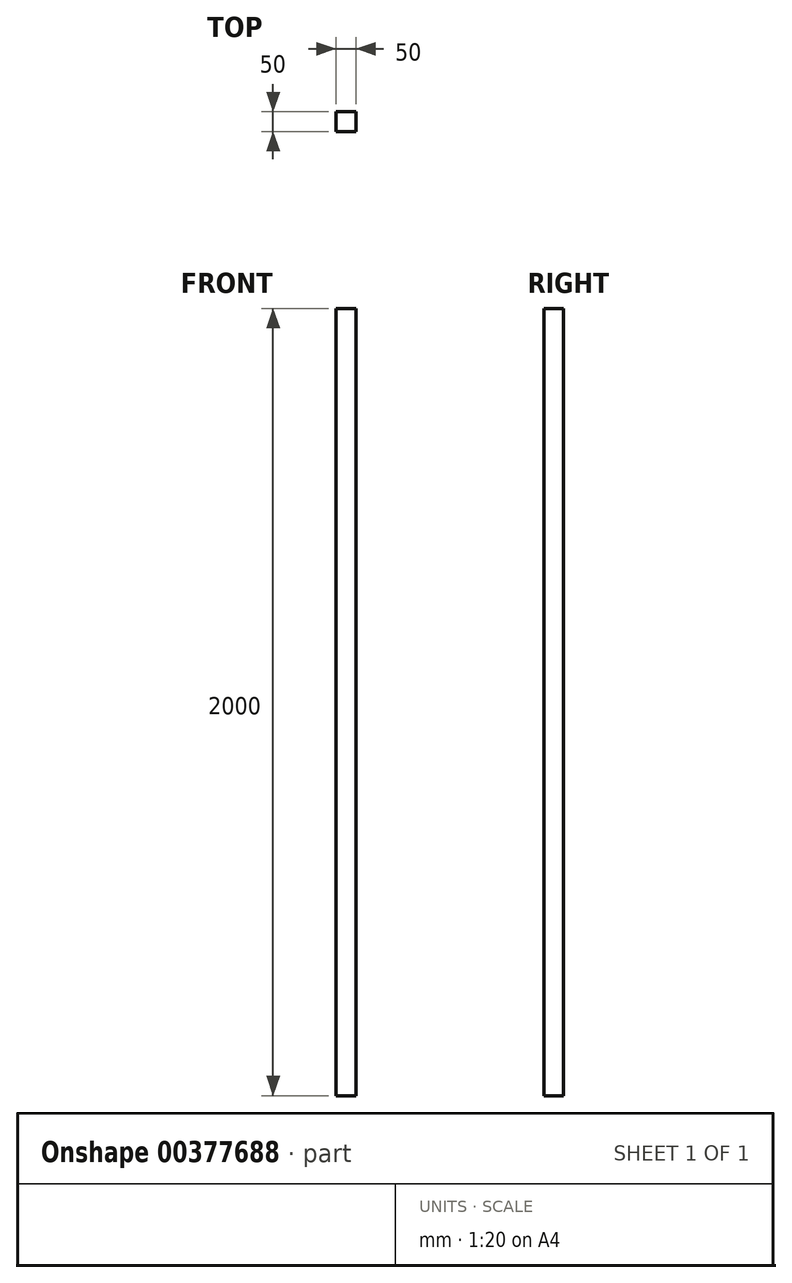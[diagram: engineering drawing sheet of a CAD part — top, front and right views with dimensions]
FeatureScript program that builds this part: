
annotation { "Feature Type Name" : "Feature", "Feature Type Description" : "" }
export const myFeature = defineFeature(function(context is Context, id is Id, definition is map)
    precondition{}
    {
        {
            var Q0;
            Q0=qCreatedBy(makeId("Top.planeOp"),FACE);
            var sketch = newSketch(context, id + "F0", { "sketchPlane" : qUnion([Q0])});
            skLineSegment(sketch, "E0.bottom", {"start": v(0, 0) * mm, "end": v(50, 0) * mm});
            skLineSegment(sketch, "E0.top", {"start": v(0, 50) * mm, "end": v(50, 50) * mm});
            skLineSegment(sketch, "E0.left", {"start": v(0, 0) * mm, "end": v(0, 50) * mm});
            skLineSegment(sketch, "E0.right", {"start": v(50, 0) * mm, "end": v(50, 50) * mm});
            skSolve(sketch);
        }
        {
            var Q0;
            Q0=makeQuery(id+"F0.imprint","IMPRINT",FACE,{"disambiguationData":[TD([[makeQuery(id+"F0.imprint","IMPRINT",EDGE,{"derivedFrom":sQuery(id+"F0.wireOp",EDGE,"E0.bottom")}),1.0]])]});
            extrude(context, id + "F1", {"entities" : qUnion([Q0]), "depth" : 2000 * mm});
        }
    });
